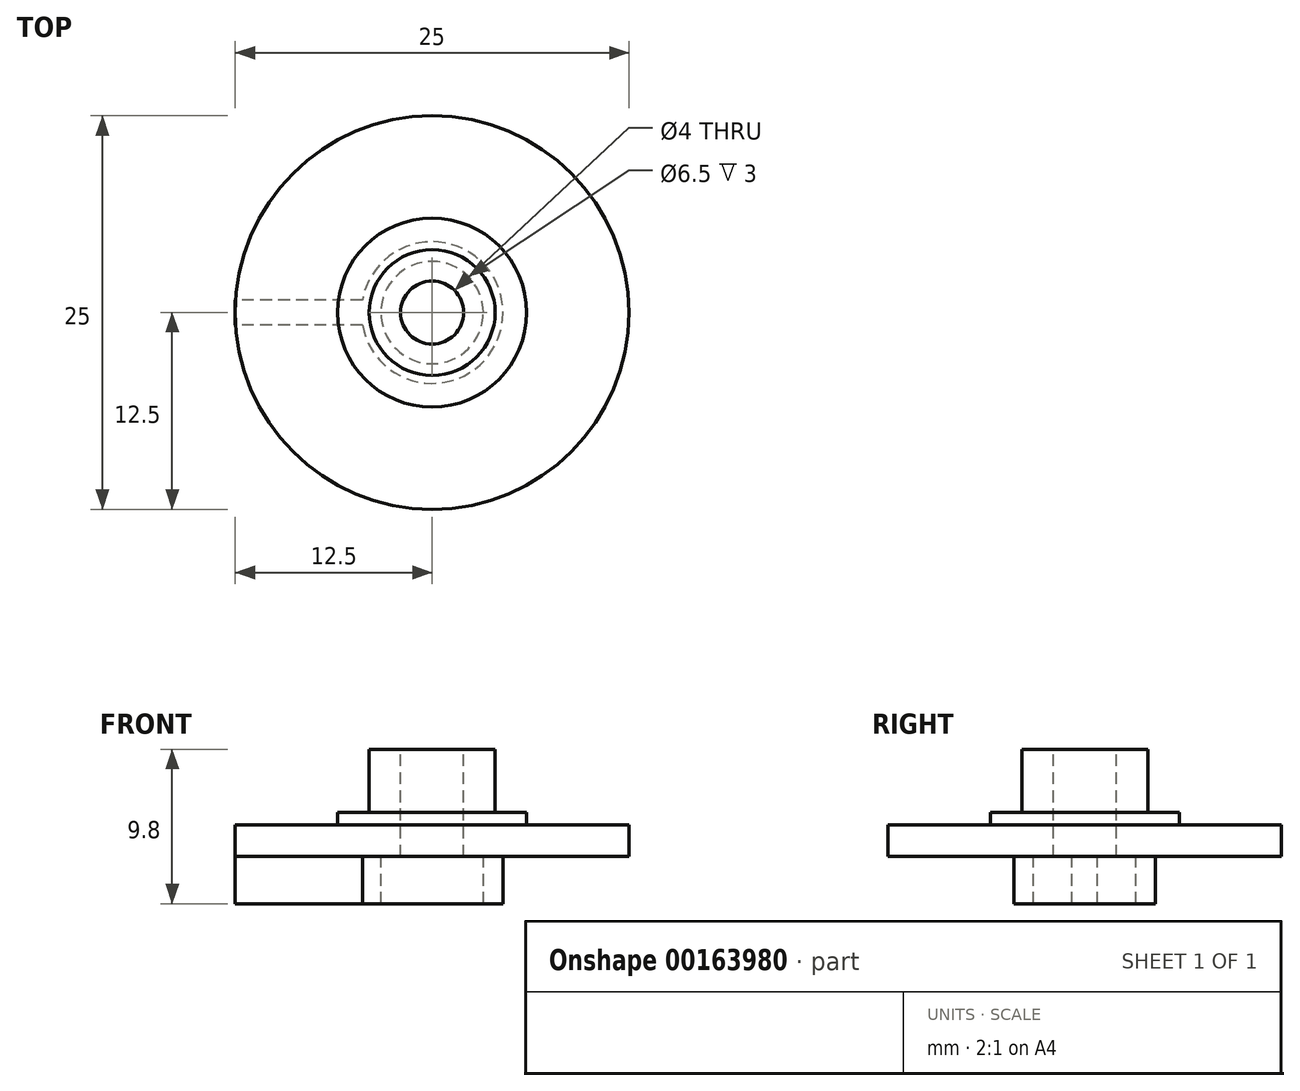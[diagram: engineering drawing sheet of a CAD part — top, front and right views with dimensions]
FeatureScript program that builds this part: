
annotation { "Feature Type Name" : "Feature", "Feature Type Description" : "" }
export const myFeature = defineFeature(function(context is Context, id is Id, definition is map)
    precondition{}
    {
        {
            var Q0;
            Q0=qCreatedBy(makeId("Top.planeOp"),FACE);
            var sketch = newSketch(context, id + "F0", { "sketchPlane" : qUnion([Q0])});
            skCircle(sketch, "E0", {"center": v(0, 0) * mm, "radius": 12.5 * mm});
            skSolve(sketch);
        }
        {
            var Q0;
            Q0=makeQuery(id+"F0.imprint","IMPRINT",FACE,{"disambiguationData":[TD([[makeQuery(id+"F0.imprint","IMPRINT",EDGE,{"derivedFrom":sQuery(id+"F0.wireOp",EDGE,"E0")}),1.0]])]});
            extrude(context, id + "F1", {"entities" : qUnion([Q0]), "depth" : 2 * mm});
        }
        {
            var Q0;
            Q0=makeQuery(id+"F1.opExtrude","CAP_FACE",FACE,{"disambiguationData":[OSD([sQuery(id+"F0.wireOp",EDGE,"E0")])],"isStart":false});
            var sketch = newSketch(context, id + "F2", { "sketchPlane" : qUnion([Q0])});
            skCircle(sketch, "E1", {"center": v(0, 0) * mm, "radius": 6 * mm});
            skSolve(sketch);
        }
        {
            var Q0;
            Q0=makeQuery(id+"F2.imprint","IMPRINT",FACE,{"disambiguationData":[TD([[makeQuery(id+"F2.imprint","IMPRINT",EDGE,{"derivedFrom":sQuery(id+"F2.wireOp",EDGE,"E1")}),1.0]])]});
            extrude(context, id + "F3", {"entities" : qUnion([Q0]), "operationType" : NewBodyOperationType.ADD, "depth" : 0.8 * mm});
        }
        {
            var Q0;
            Q0=makeQuery(id+"F3.opExtrude","CAP_FACE",FACE,{"disambiguationData":[OSD([sQuery(id+"F2.wireOp",EDGE,"E1")])],"isStart":false});
            var sketch = newSketch(context, id + "F4", { "sketchPlane" : qUnion([Q0])});
            skCircle(sketch, "E2", {"center": v(0, 0) * mm, "radius": 4 * mm});
            skSolve(sketch);
        }
        {
            var Q0;
            Q0=makeQuery(id+"F4.imprint","IMPRINT",FACE,{"disambiguationData":[TD([[makeQuery(id+"F4.imprint","IMPRINT",EDGE,{"derivedFrom":sQuery(id+"F4.wireOp",EDGE,"E2")}),1.0]])]});
            extrude(context, id + "F5", {"entities" : qUnion([Q0]), "operationType" : NewBodyOperationType.ADD, "depth" : 4 * mm});
        }
        {
            var Q0;
            Q0=makeQuery(id+"F5.opExtrude","CAP_FACE",FACE,{"disambiguationData":[OSD([sQuery(id+"F4.wireOp",EDGE,"E2")])],"isStart":false});
            var sketch = newSketch(context, id + "F6", { "sketchPlane" : qUnion([Q0])});
            skCircle(sketch, "E3", {"center": v(0, 0) * mm, "radius": 2 * mm});
            skSolve(sketch);
        }
        {
            var Q0;
            Q0=makeQuery(id+"F6.imprint","IMPRINT",FACE,{"disambiguationData":[TD([[makeQuery(id+"F6.imprint","IMPRINT",EDGE,{"derivedFrom":sQuery(id+"F6.wireOp",EDGE,"E3")}),1.0]])]});
            var Q1;
            Q1=makeQuery(id+"F1.opExtrude","CAP_FACE",FACE,{"disambiguationData":[OSD([sQuery(id+"F0.wireOp",EDGE,"E0")])],"isStart":true});
            extrude(context, id + "F7", {"entities" : qUnion([Q0]), "operationType" : NewBodyOperationType.REMOVE, "endBound" : BoundingType.UP_TO_SURFACE, "oppositeDirection" : true, "endBoundEntityFace" : qUnion([Q1]), "depth" : 25 * mm});
        }
        {
            var Q0;
            Q0=makeQuery(id+"F1.opExtrude","CAP_FACE",FACE,{"disambiguationData":[OSD([sQuery(id+"F0.wireOp",EDGE,"E0")])],"isStart":true});
            var sketch = newSketch(context, id + "F8", { "sketchPlane" : qUnion([Q0])});
            skCircle(sketch, "E4.0", {"center": v(0, 0) * mm, "radius": 3.25 * mm});
            skCircle(sketch, "E5", {"center": v(0, 0) * mm, "radius": 4.5 * mm});
            skSolve(sketch);
        }
        {
            var Q0;
            Q0=makeQuery(id+"F8.imprint","IMPRINT",FACE,{"disambiguationData":[TD([[makeQuery(id+"F8.imprint","IMPRINT",EDGE,{"derivedFrom":sQuery(id+"F8.wireOp",EDGE,"E4.0")}),-1.0]])]});
            extrude(context, id + "F9", {"entities" : qUnion([Q0]), "operationType" : NewBodyOperationType.ADD, "depth" : 3 * mm});
        }
        {
            var Q0;
            Q0=qCreatedBy(makeId("Front.planeOp"),FACE);
            var sketch = newSketch(context, id + "F10", { "sketchPlane" : qUnion([Q0])});
            skLineSegment(sketch, "E6", {"start": v(-4.3, -3) * mm, "end": v(-4.3, 0) * mm});
            skLineSegment(sketch, "E7", {"start": v(-4.3, 0) * mm, "end": v(-12.5, 0) * mm});
            skLineSegment(sketch, "E8", {"start": v(-4.3, -3) * mm, "end": v(-12.5, -3) * mm});
            skLineSegment(sketch, "E9", {"start": v(-12.5, 0) * mm, "end": v(-12.5, -3) * mm});
            skSolve(sketch);
        }
        {
            var Q0;
            Q0=makeQuery(id+"F10.imprint","IMPRINT",FACE,{"disambiguationData":[TD([[makeQuery(id+"F10.imprint","IMPRINT",EDGE,{"derivedFrom":sQuery(id+"F10.wireOp",EDGE,"E6")}),1.0]])]});
            extrude(context, id + "F11", {"entities" : qUnion([Q0]), "operationType" : NewBodyOperationType.ADD, "depth" : 0.8 * mm, "hasSecondDirection" : true, "secondDirectionOppositeDirection" : true, "secondDirectionDepth" : 0.8 * mm});
        }
    });
